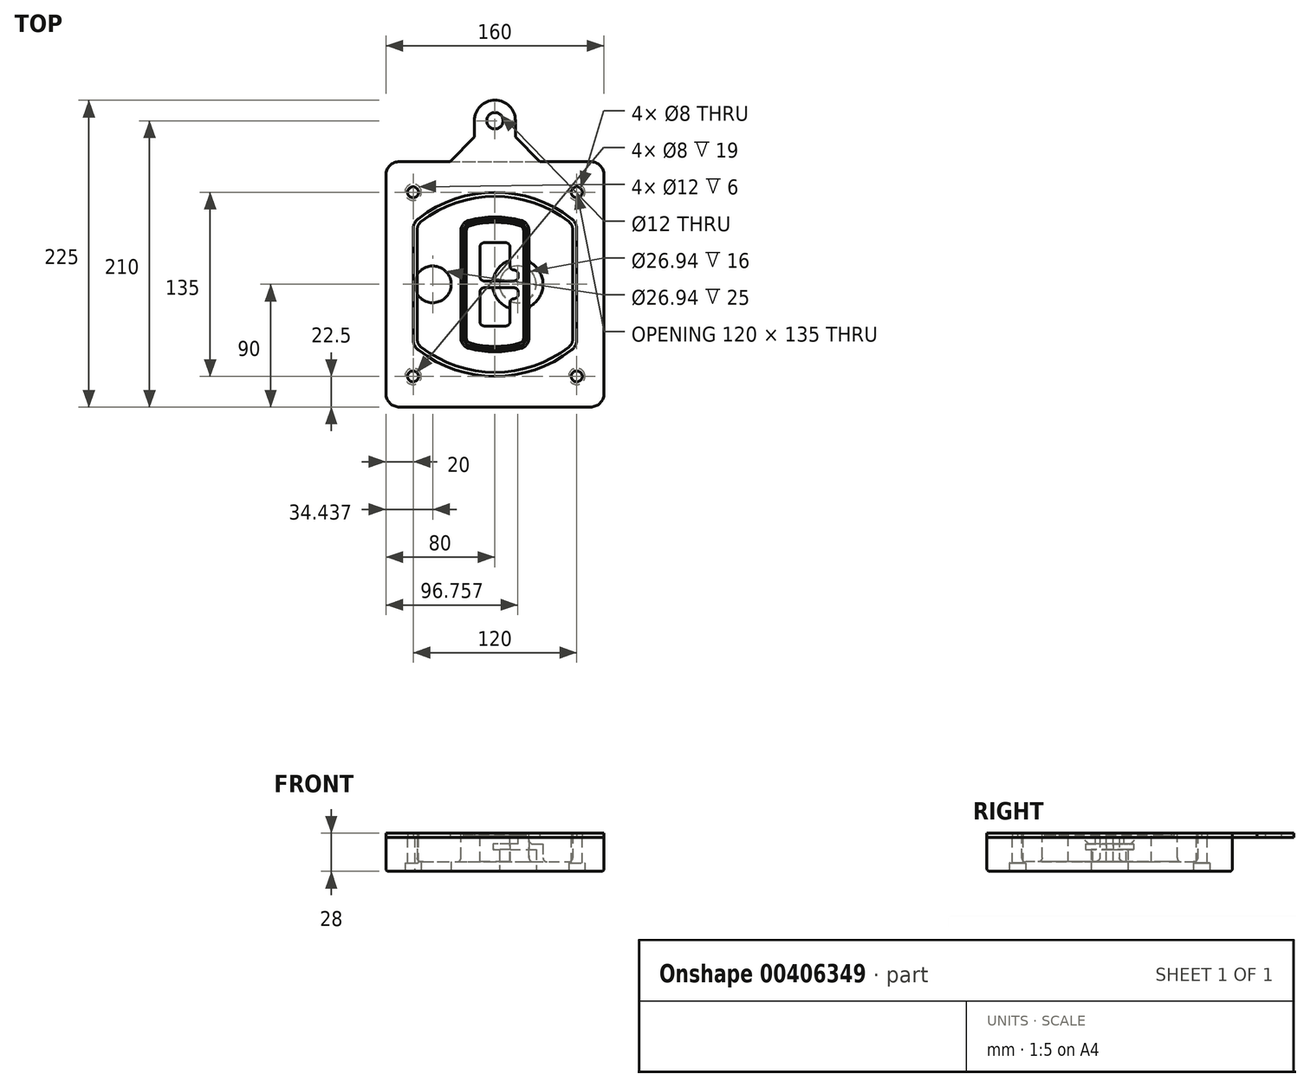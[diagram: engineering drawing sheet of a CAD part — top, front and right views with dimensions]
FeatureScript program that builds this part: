
annotation { "Feature Type Name" : "Feature", "Feature Type Description" : "" }
export const myFeature = defineFeature(function(context is Context, id is Id, definition is map)
    precondition{}
    {
        {
            var Q0;
            Q0=qCreatedBy(makeId("Top.planeOp"),FACE);
            var sketch = newSketch(context, id + "F0", { "sketchPlane" : qUnion([Q0])});
            skPoint(sketch, "E0.rect.middle", {"position": v(0, 0) * mm});
            skLineSegment(sketch, "E1.bottom", {"start": v(-70, -90) * mm, "end": v(70, -90) * mm});
            skLineSegment(sketch, "E1.top", {"start": v(-70, 90) * mm, "end": v(70, 90) * mm});
            skLineSegment(sketch, "E1.left", {"start": v(-80, -80) * mm, "end": v(-80, 80) * mm});
            skLineSegment(sketch, "E1.right", {"start": v(80, -80) * mm, "end": v(80, 80) * mm});
            skLineSegment(sketch, "E2", {"start": v(-80, 90) * mm, "end": v(80, -90) * mm, "construction": true});
            skLineSegment(sketch, "E3", {"start": v(80, 90) * mm, "end": v(-80, -90) * mm, "construction": true});
            skCircle(sketch, "E4", {"center": v(-60, 67.5) * mm, "radius": 4 * mm});
            skCircle(sketch, "E5", {"center": v(60, 67.5) * mm, "radius": 4 * mm});
            skCircle(sketch, "E6", {"center": v(60, -67.5) * mm, "radius": 4 * mm});
            skCircle(sketch, "E7", {"center": v(-60, -67.5) * mm, "radius": 4 * mm});
            skLineSegment(sketch, "E8", {"start": v(-60, 67.5) * mm, "end": v(60, 67.5) * mm, "construction": true});
            skLineSegment(sketch, "E9", {"start": v(60, 67.5) * mm, "end": v(60, -67.5) * mm, "construction": true});
            skLineSegment(sketch, "E10", {"start": v(60, -67.5) * mm, "end": v(-60, -67.5) * mm, "construction": true});
            skLineSegment(sketch, "E11", {"start": v(-60, -67.5) * mm, "end": v(-60, 67.5) * mm, "construction": true});
            skLineSegment(sketch, "E12", {"start": v(-60, 40.3) * mm, "end": v(-60, -40.3) * mm});
            skLineSegment(sketch, "E13", {"start": v(60, 40.3) * mm, "end": v(60, -40.3) * mm});
            skArc(sketch, "E14", {"start": v(56.15, 48.18) * mm, "mid": v(0, 67.5) * mm, "end": v(-56.15, 48.18) * mm});
            skArc(sketch, "E15", {"start": v(-56.15, -48.18) * mm, "mid": v(0, -67.5) * mm, "end": v(56.15, -48.18) * mm});
            skLineSegment(sketch, "E16", {"start": v(-60, 0) * mm, "end": v(60, 0) * mm, "construction": true});
            skPoint(sketch, "E17.visualSharp", {"position": v(-60, -45) * mm});
            skArc(sketch, "E17.filletArc", {"start": v(-60, -40.3) * mm, "mid": v(-58.99, -44.68) * mm, "end": v(-56.15, -48.18) * mm});
            skPoint(sketch, "E18.visualSharp", {"position": v(-60, 45) * mm});
            skArc(sketch, "E18.filletArc", {"start": v(-56.15, 48.18) * mm, "mid": v(-58.99, 44.68) * mm, "end": v(-60, 40.3) * mm});
            skPoint(sketch, "E19.visualSharp", {"position": v(60, 45) * mm});
            skArc(sketch, "E19.filletArc", {"start": v(60, 40.3) * mm, "mid": v(58.99, 44.68) * mm, "end": v(56.15, 48.18) * mm});
            skPoint(sketch, "E20.visualSharp", {"position": v(60, -45) * mm});
            skArc(sketch, "E20.filletArc", {"start": v(56.15, -48.18) * mm, "mid": v(58.99, -44.68) * mm, "end": v(60, -40.3) * mm});
            skPoint(sketch, "E21.visualSharp", {"position": v(-80, 90) * mm});
            skArc(sketch, "E21.filletArc", {"start": v(-70, 90) * mm, "mid": v(-77.07, 87.07) * mm, "end": v(-80, 80) * mm});
            skPoint(sketch, "E22.visualSharp", {"position": v(80, 90) * mm});
            skArc(sketch, "E22.filletArc", {"start": v(80, 80) * mm, "mid": v(77.07, 87.07) * mm, "end": v(70, 90) * mm});
            skPoint(sketch, "E23.visualSharp", {"position": v(80, -90) * mm});
            skArc(sketch, "E23.filletArc", {"start": v(70, -90) * mm, "mid": v(77.07, -87.07) * mm, "end": v(80, -80) * mm});
            skPoint(sketch, "E24.visualSharp", {"position": v(-80, -90) * mm});
            skArc(sketch, "E24.filletArc", {"start": v(-80, -80) * mm, "mid": v(-77.07, -87.07) * mm, "end": v(-70, -90) * mm});
            skArc(sketch, "E25.0", {"start": v(57, 40.3) * mm, "mid": v(56.3, 43.36) * mm, "end": v(54.3, 45.81) * mm});
            skLineSegment(sketch, "E25.1", {"start": v(57, 40.3) * mm, "end": v(57, -40.3) * mm});
            skArc(sketch, "E25.2", {"start": v(54.3, -45.81) * mm, "mid": v(56.3, -43.36) * mm, "end": v(57, -40.3) * mm});
            skArc(sketch, "E25.3", {"start": v(-54.3, -45.81) * mm, "mid": v(0, -64.5) * mm, "end": v(54.3, -45.81) * mm});
            skArc(sketch, "E25.4", {"start": v(-57, -40.3) * mm, "mid": v(-56.3, -43.36) * mm, "end": v(-54.3, -45.81) * mm});
            skArc(sketch, "E25.5", {"start": v(54.3, 45.81) * mm, "mid": v(0, 64.5) * mm, "end": v(-54.3, 45.81) * mm});
            skLineSegment(sketch, "E25.6", {"start": v(-57, 40.3) * mm, "end": v(-57, -40.3) * mm});
            skArc(sketch, "E25.7", {"start": v(-54.3, 45.81) * mm, "mid": v(-56.3, 43.36) * mm, "end": v(-57, 40.3) * mm});
            skArc(sketch, "E26.0", {"start": v(-58.62, 51.33) * mm, "mid": v(-62.58, 46.43) * mm, "end": v(-64, 40.3) * mm});
            skArc(sketch, "E26.1", {"start": v(58.62, 51.33) * mm, "mid": v(0, 71.5) * mm, "end": v(-58.62, 51.33) * mm});
            skArc(sketch, "E26.2", {"start": v(64, 40.3) * mm, "mid": v(62.58, 46.43) * mm, "end": v(58.62, 51.33) * mm});
            skLineSegment(sketch, "E26.3", {"start": v(64, 40.3) * mm, "end": v(64, -40.3) * mm});
            skArc(sketch, "E26.4", {"start": v(58.62, -51.33) * mm, "mid": v(62.58, -46.43) * mm, "end": v(64, -40.3) * mm});
            skLineSegment(sketch, "E26.5", {"start": v(-64, 40.3) * mm, "end": v(-64, -40.3) * mm});
            skArc(sketch, "E26.6", {"start": v(-58.62, -51.33) * mm, "mid": v(0, -71.5) * mm, "end": v(58.62, -51.33) * mm});
            skArc(sketch, "E26.7", {"start": v(-64, -40.3) * mm, "mid": v(-62.58, -46.43) * mm, "end": v(-58.62, -51.33) * mm});
            skSolve(sketch);
        }
        {
            var Q0;
            Q0=makeQuery(id+"F0.imprint","IMPRINT",FACE,{"disambiguationData":[TD([[makeQuery(id+"F0.imprint","IMPRINT",EDGE,{"derivedFrom":sQuery(id+"F0.wireOp",EDGE,"E1.bottom")}),1.0]])]});
            var Q1;
            Q1=makeQuery(id+"F0.imprint","IMPRINT",FACE,{"disambiguationData":[TD([[makeQuery(id+"F0.imprint","IMPRINT",EDGE,{"derivedFrom":sQuery(id+"F0.wireOp",EDGE,"E12")}),1.0]])]});
            var Q2;
            Q2=makeQuery(id+"F0.imprint","IMPRINT",FACE,{"disambiguationData":[TD([[makeQuery(id+"F0.imprint","IMPRINT",EDGE,{"derivedFrom":sQuery(id+"F0.wireOp",EDGE,"E25.0")}),1.0]])]});
            var Q3;
            Q3=makeQuery(id+"F0.imprint","IMPRINT",FACE,{"disambiguationData":[TD([[makeQuery(id+"F0.imprint","IMPRINT",EDGE,{"derivedFrom":sQuery(id+"F0.wireOp",EDGE,"E12")}),-1.0]])]});
            extrude(context, id + "F1", {"entities" : qUnion([Q0, Q1, Q2, Q3]), "oppositeDirection" : true, "depth" : 25 * mm});
        }
        {
            var Q0;
            Q0=makeQuery(id+"F0.imprint","IMPRINT",FACE,{"disambiguationData":[TD([[makeQuery(id+"F0.imprint","IMPRINT",EDGE,{"derivedFrom":sQuery(id+"F0.wireOp",EDGE,"E12")}),1.0]])]});
            var Q1;
            Q1 = qSketchRegion(id + "F16", true);
            extrude(context, id + "F2", {"entities" : qUnion([Q0, Q1]), "operationType" : NewBodyOperationType.ADD, "depth" : 3 * mm});
        }
        {
            var Q0;
            Q0=makeQuery(id+"F0.imprint","IMPRINT",FACE,{"disambiguationData":[TD([[makeQuery(id+"F0.imprint","IMPRINT",EDGE,{"derivedFrom":sQuery(id+"F0.wireOp",EDGE,"E25.0")}),1.0]])]});
            extrude(context, id + "F3", {"entities" : qUnion([Q0]), "operationType" : NewBodyOperationType.REMOVE, "oppositeDirection" : true, "depth" : 18 * mm});
        }
        {
            var Q0;
            Q0=makeQuery(id+"F2.opExtrude","CAP_FACE",FACE,{"disambiguationData":[OSD([sQuery(id+"F0.wireOp",EDGE,"E12"),sQuery(id+"F0.wireOp",EDGE,"E13"),sQuery(id+"F0.wireOp",EDGE,"E14"),sQuery(id+"F0.wireOp",EDGE,"E15"),sQuery(id+"F0.wireOp",EDGE,"E17.filletArc"),sQuery(id+"F0.wireOp",EDGE,"E18.filletArc"),sQuery(id+"F0.wireOp",EDGE,"E19.filletArc"),sQuery(id+"F0.wireOp",EDGE,"E20.filletArc"),sQuery(id+"F0.wireOp",EDGE,"E25.0"),sQuery(id+"F0.wireOp",EDGE,"E25.1"),sQuery(id+"F0.wireOp",EDGE,"E25.2"),sQuery(id+"F0.wireOp",EDGE,"E25.3"),sQuery(id+"F0.wireOp",EDGE,"E25.4"),sQuery(id+"F0.wireOp",EDGE,"E25.5"),sQuery(id+"F0.wireOp",EDGE,"E25.6"),sQuery(id+"F0.wireOp",EDGE,"E25.7")])],"isStart":false});
            var sketch = newSketch(context, id + "F4", { "sketchPlane" : qUnion([Q0])});
            skArc(sketch, "E27.0", {"start": v(-19.08, -46.97) * mm, "mid": v(0, -49.5) * mm, "end": v(19.08, -46.97) * mm});
            skArc(sketch, "E28.0", {"start": v(19.08, 46.97) * mm, "mid": v(0, 49.5) * mm, "end": v(-19.08, 46.97) * mm});
            skLineSegment(sketch, "E29", {"start": v(-25, 39.25) * mm, "end": v(-25, -39.25) * mm});
            skLineSegment(sketch, "E30", {"start": v(25, 39.25) * mm, "end": v(25, -39.25) * mm});
            skLineSegment(sketch, "E31", {"start": v(-25, 45.1) * mm, "end": v(25, 45.1) * mm, "construction": true});
            skLineSegment(sketch, "E32", {"start": v(-25, -45.1) * mm, "end": v(25, -45.1) * mm, "construction": true});
            skPoint(sketch, "E33.visualSharp", {"position": v(-25, 45.1) * mm});
            skArc(sketch, "E33.filletArc", {"start": v(-19.08, 46.97) * mm, "mid": v(-23.35, 44.11) * mm, "end": v(-25, 39.25) * mm});
            skPoint(sketch, "E34.visualSharp", {"position": v(25, 45.1) * mm});
            skArc(sketch, "E34.filletArc", {"start": v(25, 39.25) * mm, "mid": v(23.35, 44.11) * mm, "end": v(19.08, 46.97) * mm});
            skPoint(sketch, "E35.visualSharp", {"position": v(25, -45.1) * mm});
            skArc(sketch, "E35.filletArc", {"start": v(19.08, -46.97) * mm, "mid": v(23.35, -44.11) * mm, "end": v(25, -39.25) * mm});
            skPoint(sketch, "E36.visualSharp", {"position": v(-25, -45.1) * mm});
            skArc(sketch, "E36.filletArc", {"start": v(-25, -39.25) * mm, "mid": v(-23.35, -44.11) * mm, "end": v(-19.08, -46.97) * mm});
            skArc(sketch, "E37.0", {"start": v(54.3, 45.81) * mm, "mid": v(0, 64.5) * mm, "end": v(-54.3, 45.81) * mm});
            skArc(sketch, "E37.1", {"start": v(-54.3, 45.81) * mm, "mid": v(-56.3, 43.36) * mm, "end": v(-57, 40.3) * mm});
            skLineSegment(sketch, "E37.2", {"start": v(-57, 40.3) * mm, "end": v(-57, -40.3) * mm});
            skArc(sketch, "E37.3", {"start": v(-57, -40.3) * mm, "mid": v(-56.3, -43.36) * mm, "end": v(-54.3, -45.81) * mm});
            skArc(sketch, "E37.4", {"start": v(-54.3, -45.81) * mm, "mid": v(0, -64.5) * mm, "end": v(54.3, -45.81) * mm});
            skArc(sketch, "E37.5", {"start": v(54.3, -45.81) * mm, "mid": v(56.3, -43.36) * mm, "end": v(57, -40.3) * mm});
            skLineSegment(sketch, "E37.6", {"start": v(57, 40.3) * mm, "end": v(57, -40.3) * mm});
            skArc(sketch, "E37.7", {"start": v(57, 40.3) * mm, "mid": v(56.3, 43.36) * mm, "end": v(54.3, 45.81) * mm});
            skLineSegment(sketch, "E38.0", {"start": v(23, 39.25) * mm, "end": v(23, -39.25) * mm});
            skArc(sketch, "E38.1", {"start": v(18.56, -45.04) * mm, "mid": v(21.76, -42.9) * mm, "end": v(23, -39.25) * mm});
            skArc(sketch, "E38.2", {"start": v(-18.56, -45.04) * mm, "mid": v(0, -47.5) * mm, "end": v(18.56, -45.04) * mm});
            skArc(sketch, "E38.3", {"start": v(-23, -39.25) * mm, "mid": v(-21.76, -42.9) * mm, "end": v(-18.56, -45.04) * mm});
            skLineSegment(sketch, "E38.4", {"start": v(-23, 39.25) * mm, "end": v(-23, -39.25) * mm});
            skArc(sketch, "E38.5", {"start": v(23, 39.25) * mm, "mid": v(21.76, 42.9) * mm, "end": v(18.56, 45.04) * mm});
            skArc(sketch, "E38.6", {"start": v(-18.56, 45.04) * mm, "mid": v(-21.76, 42.9) * mm, "end": v(-23, 39.25) * mm});
            skArc(sketch, "E38.7", {"start": v(18.56, 45.04) * mm, "mid": v(0, 47.5) * mm, "end": v(-18.56, 45.04) * mm});
            skArc(sketch, "E39.0", {"start": v(21, 39.25) * mm, "mid": v(20.18, 41.68) * mm, "end": v(18.04, 43.1) * mm});
            skLineSegment(sketch, "E39.1", {"start": v(21, 39.25) * mm, "end": v(21, -39.25) * mm});
            skArc(sketch, "E39.2", {"start": v(18.04, -43.1) * mm, "mid": v(20.18, -41.68) * mm, "end": v(21, -39.25) * mm});
            skArc(sketch, "E39.3", {"start": v(-18.04, -43.1) * mm, "mid": v(0, -45.5) * mm, "end": v(18.04, -43.1) * mm});
            skArc(sketch, "E39.4", {"start": v(-21, -39.25) * mm, "mid": v(-20.18, -41.68) * mm, "end": v(-18.04, -43.1) * mm});
            skArc(sketch, "E39.5", {"start": v(18.04, 43.1) * mm, "mid": v(0, 45.5) * mm, "end": v(-18.04, 43.1) * mm});
            skLineSegment(sketch, "E39.6", {"start": v(-21, 39.25) * mm, "end": v(-21, -39.25) * mm});
            skArc(sketch, "E39.7", {"start": v(-18.04, 43.1) * mm, "mid": v(-20.18, 41.68) * mm, "end": v(-21, 39.25) * mm});
            skLineSegment(sketch, "E40", {"start": v(-25, 0) * mm, "end": v(25, 0) * mm, "construction": true});
            skLineSegment(sketch, "E41", {"start": v(-11, 5.5) * mm, "end": v(-11, 27.5) * mm});
            skLineSegment(sketch, "E42", {"start": v(-8, 30.5) * mm, "end": v(8, 30.5) * mm});
            skLineSegment(sketch, "E43", {"start": v(11, 27.5) * mm, "end": v(11, 13.5) * mm});
            skLineSegment(sketch, "E44", {"start": v(14, 10.5) * mm, "end": v(14, 10.5) * mm});
            skLineSegment(sketch, "E45", {"start": v(17, 7.5) * mm, "end": v(17, 5.5) * mm});
            skLineSegment(sketch, "E46", {"start": v(14, 2.5) * mm, "end": v(-8, 2.5) * mm});
            skPoint(sketch, "E47.visualSharp", {"position": v(-11, 30.5) * mm});
            skArc(sketch, "E47.filletArc", {"start": v(-8, 30.5) * mm, "mid": v(-10.12, 29.62) * mm, "end": v(-11, 27.5) * mm});
            skPoint(sketch, "E48.visualSharp", {"position": v(11, 30.5) * mm});
            skArc(sketch, "E48.filletArc", {"start": v(11, 27.5) * mm, "mid": v(10.12, 29.62) * mm, "end": v(8, 30.5) * mm});
            skPoint(sketch, "E49.visualSharp", {"position": v(11, 10.5) * mm});
            skArc(sketch, "E49.filletArc", {"start": v(11, 13.5) * mm, "mid": v(11.88, 11.38) * mm, "end": v(14, 10.5) * mm});
            skPoint(sketch, "E50.visualSharp", {"position": v(17, 10.5) * mm});
            skArc(sketch, "E50.filletArc", {"start": v(17, 7.5) * mm, "mid": v(16.12, 9.62) * mm, "end": v(14, 10.5) * mm});
            skPoint(sketch, "E51.visualSharp", {"position": v(17, 2.5) * mm});
            skArc(sketch, "E51.filletArc", {"start": v(14, 2.5) * mm, "mid": v(16.12, 3.38) * mm, "end": v(17, 5.5) * mm});
            skPoint(sketch, "E52.visualSharp", {"position": v(-11, 2.5) * mm});
            skArc(sketch, "E52.filletArc", {"start": v(-11, 5.5) * mm, "mid": v(-10.12, 3.38) * mm, "end": v(-8, 2.5) * mm});
            skLineSegment(sketch, "E53.0.MirrorCS", {"start": v(14, -2.5) * mm, "end": v(-8, -2.5) * mm});
            skArc(sketch, "E54.0.MirrorCS", {"start": v(-11, -5.5) * mm, "mid": v(-10.12, -3.38) * mm, "end": v(-8, -2.5) * mm});
            skLineSegment(sketch, "E55.0.MirrorCS", {"start": v(-11, -5.5) * mm, "end": v(-11, -27.5) * mm});
            skArc(sketch, "E56.0.MirrorCS", {"start": v(-8, -30.5) * mm, "mid": v(-10.12, -29.62) * mm, "end": v(-11, -27.5) * mm});
            skLineSegment(sketch, "E57.0.MirrorCS", {"start": v(-8, -30.5) * mm, "end": v(8, -30.5) * mm});
            skArc(sketch, "E58.0.MirrorCS", {"start": v(11, -27.5) * mm, "mid": v(10.12, -29.62) * mm, "end": v(8, -30.5) * mm});
            skLineSegment(sketch, "E59.0.MirrorCS", {"start": v(11, -27.5) * mm, "end": v(11, -13.5) * mm});
            skArc(sketch, "E60.0.MirrorCS", {"start": v(11, -13.5) * mm, "mid": v(11.88, -11.38) * mm, "end": v(14, -10.5) * mm});
            skArc(sketch, "E61.0.MirrorCS", {"start": v(17, -7.5) * mm, "mid": v(16.12, -9.62) * mm, "end": v(14, -10.5) * mm});
            skLineSegment(sketch, "E62.0.MirrorCS", {"start": v(17, -7.5) * mm, "end": v(17, -5.5) * mm});
            skArc(sketch, "E63.0.MirrorCS", {"start": v(14, -2.5) * mm, "mid": v(16.12, -3.38) * mm, "end": v(17, -5.5) * mm});
            skSolve(sketch);
        }
        {
            var Q0;
            Q0=makeQuery(id+"F4.imprint","IMPRINT",FACE,{"disambiguationData":[TD([[makeQuery(id+"F4.imprint","IMPRINT",EDGE,{"derivedFrom":sQuery(id+"F4.wireOp",EDGE,"E27.0")}),1.0]])]});
            var Q1;
            Q1=makeQuery(id+"F4.imprint","IMPRINT",FACE,{"disambiguationData":[TD([[makeQuery(id+"F4.imprint","IMPRINT",EDGE,{"derivedFrom":sQuery(id+"F4.wireOp",EDGE,"E38.0")}),-1.0]])]});
            var Q2;
            Q2=makeQuery(id+"F4.imprint","IMPRINT",FACE,{"disambiguationData":[TD([[makeQuery(id+"F4.imprint","IMPRINT",EDGE,{"derivedFrom":sQuery(id+"F4.wireOp",EDGE,"E39.0")}),1.0]])]});
            extrude(context, id + "F5", {"entities" : qUnion([Q0, Q1, Q2]), "operationType" : NewBodyOperationType.ADD, "endBound" : BoundingType.UP_TO_NEXT, "oppositeDirection" : true, "depth" : 25 * mm});
        }
        {
            var Q0;
            Q0=makeQuery(id+"F4.imprint","IMPRINT",FACE,{"disambiguationData":[TD([[makeQuery(id+"F4.imprint","IMPRINT",EDGE,{"derivedFrom":sQuery(id+"F4.wireOp",EDGE,"E38.0")}),-1.0]])]});
            extrude(context, id + "F6", {"entities" : qUnion([Q0]), "operationType" : NewBodyOperationType.REMOVE, "oppositeDirection" : true, "depth" : 2 * mm});
        }
        {
            var Q0;
            Q0=makeQuery(id+"F1.opExtrude","CAP_FACE",FACE,{"disambiguationData":[OSD([sQuery(id+"F0.wireOp",EDGE,"E1.bottom"),sQuery(id+"F0.wireOp",EDGE,"E1.top"),sQuery(id+"F0.wireOp",EDGE,"E1.left"),sQuery(id+"F0.wireOp",EDGE,"E1.right"),sQuery(id+"F0.wireOp",EDGE,"E4"),sQuery(id+"F0.wireOp",EDGE,"E5"),sQuery(id+"F0.wireOp",EDGE,"E6"),sQuery(id+"F0.wireOp",EDGE,"E7"),sQuery(id+"F0.wireOp",EDGE,"E21.filletArc"),sQuery(id+"F0.wireOp",EDGE,"E22.filletArc"),sQuery(id+"F0.wireOp",EDGE,"E23.filletArc"),sQuery(id+"F0.wireOp",EDGE,"E24.filletArc")])],"isStart":false});
            var sketch = newSketch(context, id + "F7", { "sketchPlane" : qUnion([Q0])});
            skCircle(sketch, "E64", {"center": v(16.76, 0) * mm, "radius": 13.47 * mm});
            skCircle(sketch, "E65", {"center": v(-45.56, 0) * mm, "radius": 13.47 * mm});
            skLineSegment(sketch, "E66", {"start": v(80, 0) * mm, "end": v(-80, 0) * mm});
            skCircle(sketch, "E67", {"center": v(16.76, 0) * mm, "radius": 18.47 * mm});
            skCircle(sketch, "E68", {"center": v(60, -67.5) * mm, "radius": 6 * mm});
            skCircle(sketch, "E69", {"center": v(-60, -67.5) * mm, "radius": 6 * mm});
            skCircle(sketch, "E70", {"center": v(-60, 67.5) * mm, "radius": 6 * mm});
            skCircle(sketch, "E71", {"center": v(60, 67.5) * mm, "radius": 6 * mm});
            skSolve(sketch);
        }
        {
            var Q0;
            {var subQ1=sQuery(id+"F7.wireOp",EDGE,"E66");var subQ4=sQuery(id+"F7.wireOp",EDGE,"E64");var subQ6=makeQuery(id+"F7.imprint","INTERSECT",VERTEX,{"disambiguationData":[OD(0.0)],"derivedFrom":[subQ4,subQ1]});Q0=makeQuery(id+"F7.imprint","IMPRINT",FACE,{"disambiguationData":[TD([[makeQuery(id+"F7.imprint","IMPRINT",EDGE,{"disambiguationData":[TD([[subQ6,-1.0]])],"derivedFrom":subQ4}),-1.0]])]});}
            var Q1;
            {var subQ0=sQuery(id+"F7.wireOp",EDGE,"E66");var subQ1=sQuery(id+"F7.wireOp",EDGE,"E64");var subQ3=makeQuery(id+"F7.imprint","INTERSECT",VERTEX,{"disambiguationData":[OD(0.0)],"derivedFrom":[subQ1,subQ0]});Q1=makeQuery(id+"F7.imprint","IMPRINT",FACE,{"disambiguationData":[TD([[makeQuery(id+"F7.imprint","IMPRINT",EDGE,{"disambiguationData":[TD([[subQ3,-1.0]])],"derivedFrom":subQ1}),1.0]])]});}
            var Q2;
            {var subQ0=sQuery(id+"F7.wireOp",EDGE,"E66");var subQ1=sQuery(id+"F7.wireOp",EDGE,"E64");var subQ3=makeQuery(id+"F7.imprint","INTERSECT",VERTEX,{"disambiguationData":[OD(0.0)],"derivedFrom":[subQ1,subQ0]});Q2=makeQuery(id+"F7.imprint","IMPRINT",FACE,{"disambiguationData":[TD([[makeQuery(id+"F7.imprint","IMPRINT",EDGE,{"disambiguationData":[TD([[subQ3,1.0]])],"derivedFrom":subQ1}),1.0]])]});}
            var Q3;
            {var subQ1=sQuery(id+"F7.wireOp",EDGE,"E66");var subQ4=sQuery(id+"F7.wireOp",EDGE,"E64");var subQ6=makeQuery(id+"F7.imprint","INTERSECT",VERTEX,{"disambiguationData":[OD(0.0)],"derivedFrom":[subQ4,subQ1]});Q3=makeQuery(id+"F7.imprint","IMPRINT",FACE,{"disambiguationData":[TD([[makeQuery(id+"F7.imprint","IMPRINT",EDGE,{"disambiguationData":[TD([[subQ6,1.0]])],"derivedFrom":subQ4}),-1.0]])]});}
            extrude(context, id + "F8", {"entities" : qUnion([Q0, Q1, Q2, Q3]), "operationType" : NewBodyOperationType.ADD, "oppositeDirection" : true, "depth" : 20 * mm});
        }
        {
            var Q0;
            {var subQ0=sQuery(id+"F7.wireOp",EDGE,"E66");var subQ1=sQuery(id+"F7.wireOp",EDGE,"E64");var subQ3=makeQuery(id+"F7.imprint","INTERSECT",VERTEX,{"disambiguationData":[OD(0.0)],"derivedFrom":[subQ1,subQ0]});Q0=makeQuery(id+"F7.imprint","IMPRINT",FACE,{"disambiguationData":[TD([[makeQuery(id+"F7.imprint","IMPRINT",EDGE,{"disambiguationData":[TD([[subQ3,-1.0]])],"derivedFrom":subQ1}),1.0]])]});}
            var Q1;
            {var subQ0=sQuery(id+"F7.wireOp",EDGE,"E66");var subQ1=sQuery(id+"F7.wireOp",EDGE,"E64");var subQ3=makeQuery(id+"F7.imprint","INTERSECT",VERTEX,{"disambiguationData":[OD(0.0)],"derivedFrom":[subQ1,subQ0]});Q1=makeQuery(id+"F7.imprint","IMPRINT",FACE,{"disambiguationData":[TD([[makeQuery(id+"F7.imprint","IMPRINT",EDGE,{"disambiguationData":[TD([[subQ3,1.0]])],"derivedFrom":subQ1}),1.0]])]});}
            extrude(context, id + "F9", {"entities" : qUnion([Q0, Q1]), "operationType" : NewBodyOperationType.REMOVE, "oppositeDirection" : true, "depth" : 16 * mm});
        }
        {
            var Q0;
            {var subQ0=sQuery(id+"F7.wireOp",EDGE,"E66");var subQ1=sQuery(id+"F7.wireOp",EDGE,"E65");var subQ3=makeQuery(id+"F7.imprint","INTERSECT",VERTEX,{"disambiguationData":[OD(0.0)],"derivedFrom":[subQ1,subQ0]});Q0=makeQuery(id+"F7.imprint","IMPRINT",FACE,{"disambiguationData":[TD([[makeQuery(id+"F7.imprint","IMPRINT",EDGE,{"disambiguationData":[TD([[subQ3,-1.0]])],"derivedFrom":subQ1}),1.0]])]});}
            var Q1;
            {var subQ0=sQuery(id+"F7.wireOp",EDGE,"E66");var subQ1=sQuery(id+"F7.wireOp",EDGE,"E65");var subQ3=makeQuery(id+"F7.imprint","INTERSECT",VERTEX,{"disambiguationData":[OD(0.0)],"derivedFrom":[subQ1,subQ0]});Q1=makeQuery(id+"F7.imprint","IMPRINT",FACE,{"disambiguationData":[TD([[makeQuery(id+"F7.imprint","IMPRINT",EDGE,{"disambiguationData":[TD([[subQ3,1.0]])],"derivedFrom":subQ1}),1.0]])]});}
            extrude(context, id + "F10", {"entities" : qUnion([Q0, Q1]), "operationType" : NewBodyOperationType.REMOVE, "oppositeDirection" : true, "depth" : 25 * mm});
        }
        {
            var Q0;
            Q0=makeQuery(id+"F7.imprint","IMPRINT",FACE,{"disambiguationData":[TD([[makeQuery(id+"F7.imprint","IMPRINT",EDGE,{"derivedFrom":sQuery(id+"F7.wireOp",EDGE,"E68")}),1.0]])]});
            var Q1;
            Q1=makeQuery(id+"F7.imprint","IMPRINT",FACE,{"disambiguationData":[TD([[makeQuery(id+"F7.imprint","IMPRINT",EDGE,{"derivedFrom":makeQuery(id+"F1.opExtrude","CAP_EDGE",EDGE,{"disambiguationData":[OSD([sQuery(id+"F0.wireOp",EDGE,"E5")])],"isStart":false})}),-1.0]])]});
            var Q2;
            Q2=makeQuery(id+"F7.imprint","IMPRINT",FACE,{"disambiguationData":[TD([[makeQuery(id+"F7.imprint","IMPRINT",EDGE,{"derivedFrom":sQuery(id+"F7.wireOp",EDGE,"E69")}),1.0]])]});
            var Q3;
            Q3=makeQuery(id+"F7.imprint","IMPRINT",FACE,{"disambiguationData":[TD([[makeQuery(id+"F7.imprint","IMPRINT",EDGE,{"derivedFrom":makeQuery(id+"F1.opExtrude","CAP_EDGE",EDGE,{"disambiguationData":[OSD([sQuery(id+"F0.wireOp",EDGE,"E4")])],"isStart":false})}),-1.0]])]});
            var Q4;
            Q4=makeQuery(id+"F7.imprint","IMPRINT",FACE,{"disambiguationData":[TD([[makeQuery(id+"F7.imprint","IMPRINT",EDGE,{"derivedFrom":sQuery(id+"F7.wireOp",EDGE,"E70")}),1.0]])]});
            var Q5;
            Q5=makeQuery(id+"F7.imprint","IMPRINT",FACE,{"disambiguationData":[TD([[makeQuery(id+"F7.imprint","IMPRINT",EDGE,{"derivedFrom":makeQuery(id+"F1.opExtrude","CAP_EDGE",EDGE,{"disambiguationData":[OSD([sQuery(id+"F0.wireOp",EDGE,"E7")])],"isStart":false})}),-1.0]])]});
            var Q6;
            Q6=makeQuery(id+"F7.imprint","IMPRINT",FACE,{"disambiguationData":[TD([[makeQuery(id+"F7.imprint","IMPRINT",EDGE,{"derivedFrom":sQuery(id+"F7.wireOp",EDGE,"E71")}),1.0]])]});
            var Q7;
            Q7=makeQuery(id+"F7.imprint","IMPRINT",FACE,{"disambiguationData":[TD([[makeQuery(id+"F7.imprint","IMPRINT",EDGE,{"derivedFrom":makeQuery(id+"F1.opExtrude","CAP_EDGE",EDGE,{"disambiguationData":[OSD([sQuery(id+"F0.wireOp",EDGE,"E6")])],"isStart":false})}),-1.0]])]});
            extrude(context, id + "F11", {"entities" : qUnion([Q0, Q1, Q2, Q3, Q4, Q5, Q6, Q7]), "operationType" : NewBodyOperationType.REMOVE, "oppositeDirection" : true, "depth" : 6 * mm});
        }
        {
            var Q0;
            Q0=makeQuery(id+"F9.boolean.opBoolean","COPY",FACE,{"derivedFrom":makeQuery(id+"F9.opExtrude","CAP_FACE",FACE,{"disambiguationData":[OSD([sQuery(id+"F7.wireOp",EDGE,"E64")])],"isStart":false})});
            var sketch = newSketch(context, id + "F12", { "sketchPlane" : qUnion([Q0])});
            skArc(sketch, "E72.0", {"start": v(11, 17.55) * mm, "mid": v(2.57, 11.82) * mm, "end": v(-1.54, 2.5) * mm});
            skArc(sketch, "E72.1", {"start": v(-1.54, -2.5) * mm, "mid": v(2.57, -11.82) * mm, "end": v(11, -17.55) * mm});
            skLineSegment(sketch, "E73", {"start": v(-1.54, -2.5) * mm, "end": v(14, -2.5) * mm});
            skLineSegment(sketch, "E74.0", {"start": v(14, 2.5) * mm, "end": v(-1.54, 2.5) * mm});
            skArc(sketch, "E74.1", {"start": v(14, 2.5) * mm, "mid": v(16.12, 3.38) * mm, "end": v(17, 5.5) * mm});
            skLineSegment(sketch, "E74.2", {"start": v(17, 7.5) * mm, "end": v(17, 5.5) * mm});
            skArc(sketch, "E74.3", {"start": v(17, 7.5) * mm, "mid": v(16.12, 9.62) * mm, "end": v(14, 10.5) * mm});
            skArc(sketch, "E74.4", {"start": v(11, 13.5) * mm, "mid": v(11.88, 11.38) * mm, "end": v(14, 10.5) * mm});
            skLineSegment(sketch, "E74.5", {"start": v(11, 17.55) * mm, "end": v(11, 13.5) * mm});
            skLineSegment(sketch, "E74.7", {"start": v(14, -2.5) * mm, "end": v(-1.54, -2.5) * mm});
            skArc(sketch, "E74.8", {"start": v(14, -2.5) * mm, "mid": v(16.12, -3.38) * mm, "end": v(17, -5.5) * mm});
            skLineSegment(sketch, "E74.9", {"start": v(17, -7.5) * mm, "end": v(17, -5.5) * mm});
            skArc(sketch, "E74.10", {"start": v(17, -7.5) * mm, "mid": v(16.12, -9.62) * mm, "end": v(14, -10.5) * mm});
            skArc(sketch, "E74.11", {"start": v(11, -13.5) * mm, "mid": v(11.88, -11.38) * mm, "end": v(14, -10.5) * mm});
            skLineSegment(sketch, "E74.12", {"start": v(11, -17.55) * mm, "end": v(11, -13.5) * mm});
            skPoint(sketch, "E75.orphan", {"position": v(11, -27.5) * mm});
            skPoint(sketch, "E76.orphan", {"position": v(-8, -2.5) * mm});
            skPoint(sketch, "E77.orphan", {"position": v(-8, 2.5) * mm});
            skPoint(sketch, "E78.orphan", {"position": v(11, 27.5) * mm});
            skSolve(sketch);
        }
        {
            var Q0;
            {var subQ7=sQuery(id+"F12.wireOp",EDGE,"E72.0");var subQ14=sQuery(id+"F12.wireOp",EDGE,"E72.1");var subQ16=sQuery(id+"F12.wireOp",EDGE,"E74.1");var subQ18=sQuery(id+"F12.wireOp",EDGE,"E74.8");Q0=qUnion([makeQuery(id+"F12.imprint","IMPRINT",FACE,{"disambiguationData":[TD([[makeQuery(id+"F12.imprint","IMPRINT",EDGE,{"derivedFrom":subQ7}),1.0]])]}),makeQuery(id+"F12.imprint","IMPRINT",FACE,{"disambiguationData":[TD([[makeQuery(id+"F12.imprint","IMPRINT",EDGE,{"derivedFrom":subQ14}),1.0]])]}),makeQuery(id+"F12.imprint","IMPRINT",FACE,{"disambiguationData":[TD([[makeQuery(id+"F12.imprint","IMPRINT",EDGE,{"derivedFrom":subQ16}),1.0]])]}),makeQuery(id+"F12.imprint","IMPRINT",FACE,{"disambiguationData":[TD([[makeQuery(id+"F12.imprint","IMPRINT",EDGE,{"derivedFrom":subQ18}),-1.0]])]})]);}
            var Q1;
            Q1=makeQuery(id+"F5.boolean.opBoolean","SPLIT",FACE,{"disambiguationData":[TD([makeQuery(id+"F5.opExtrude","SWEPT_FACE",FACE,{"disambiguationData":[OSD([sQuery(id+"F4.wireOp",EDGE,"E41")])]})])],"derivedFrom":makeQuery(id+"F3.boolean.opBoolean","COPY",FACE,{"derivedFrom":makeQuery(id+"F3.opExtrude","CAP_FACE",FACE,{"disambiguationData":[OSD([sQuery(id+"F0.wireOp",EDGE,"E25.0"),sQuery(id+"F0.wireOp",EDGE,"E25.1"),sQuery(id+"F0.wireOp",EDGE,"E25.2"),sQuery(id+"F0.wireOp",EDGE,"E25.3"),sQuery(id+"F0.wireOp",EDGE,"E25.4"),sQuery(id+"F0.wireOp",EDGE,"E25.5"),sQuery(id+"F0.wireOp",EDGE,"E25.6"),sQuery(id+"F0.wireOp",EDGE,"E25.7")])],"isStart":false})})});
            extrude(context, id + "F13", {"entities" : qUnion([Q0]), "operationType" : NewBodyOperationType.REMOVE, "endBound" : BoundingType.UP_TO_SURFACE, "endBoundEntityFace" : qUnion([Q1]), "depth" : 25 * mm});
        }
        {
            var Q0;
            Q0=makeQuery(id+"F3.boolean.opBoolean","COPY",EDGE,{"derivedFrom":makeQuery(id+"F3.opExtrude","CAP_EDGE",EDGE,{"disambiguationData":[OSD([sQuery(id+"F0.wireOp",EDGE,"E25.6")])],"isStart":false})});
            var Q1;
            Q1=makeQuery(id+"F8.boolean.opBoolean","INTERSECT",EDGE,{"derivedFrom":[makeQuery(id+"F5.opExtrude","SWEPT_FACE",FACE,{"disambiguationData":[OSD([sQuery(id+"F4.wireOp",EDGE,"E30")])]}),makeQuery(id+"F8.opExtrude","CAP_FACE",FACE,{"disambiguationData":[OSD([sQuery(id+"F7.wireOp",EDGE,"E67")])],"isStart":false})]});
            var Q2;
            Q2=makeQuery(id+"F8.boolean.opBoolean","INTERSECT",EDGE,{"disambiguationData":[OD(1.0)],"derivedFrom":[makeQuery(id+"F5.opExtrude","SWEPT_FACE",FACE,{"disambiguationData":[OSD([sQuery(id+"F4.wireOp",EDGE,"E30")])]}),makeQuery(id+"F8.opExtrude","SWEPT_FACE",FACE,{"disambiguationData":[OSD([sQuery(id+"F7.wireOp",EDGE,"E67")])]})]});
            var Q3;
            {var subQ0=sQuery(id+"F4.wireOp",EDGE,"E30");Q3=makeQuery(id+"F8.boolean.opBoolean","SPLIT",EDGE,{"disambiguationData":[TD([makeQuery(id+"F5.opExtrude","SWEPT_FACE",FACE,{"disambiguationData":[OSD([sQuery(id+"F4.wireOp",EDGE,"E35.filletArc")])]})])],"derivedFrom":makeQuery(id+"F5.opExtrude","CAP_EDGE",EDGE,{"disambiguationData":[OSD([subQ0])],"isStart":false})});}
            var Q4;
            {var subQ0=sQuery(id+"F0.wireOp",EDGE,"E25.7");var subQ1=sQuery(id+"F0.wireOp",EDGE,"E25.1");var subQ2=sQuery(id+"F0.wireOp",EDGE,"E25.6");var subQ3=sQuery(id+"F0.wireOp",EDGE,"E25.5");var subQ4=sQuery(id+"F0.wireOp",EDGE,"E25.4");var subQ5=sQuery(id+"F0.wireOp",EDGE,"E25.0");var subQ6=sQuery(id+"F0.wireOp",EDGE,"E25.2");var subQ7=sQuery(id+"F0.wireOp",EDGE,"E25.3");Q4=makeQuery(id+"F8.boolean.opBoolean","INTERSECT",EDGE,{"derivedFrom":[makeQuery(id+"F5.boolean.opBoolean","SPLIT",FACE,{"disambiguationData":[TD([makeQuery(id+"F2.opExtrude","SWEPT_FACE",FACE,{"disambiguationData":[OSD([subQ5])]})])],"derivedFrom":makeQuery(id+"F3.boolean.opBoolean","COPY",FACE,{"derivedFrom":makeQuery(id+"F3.opExtrude","CAP_FACE",FACE,{"disambiguationData":[OSD([subQ5,subQ1,subQ6,subQ7,subQ4,subQ3,subQ2,subQ0])],"isStart":false})})}),makeQuery(id+"F8.opExtrude","SWEPT_FACE",FACE,{"disambiguationData":[OSD([sQuery(id+"F7.wireOp",EDGE,"E67")])]})]});}
            var Q5;
            Q5=makeQuery(id+"F8.boolean.opBoolean","INTERSECT",EDGE,{"disambiguationData":[OD(0.0)],"derivedFrom":[makeQuery(id+"F5.opExtrude","SWEPT_FACE",FACE,{"disambiguationData":[OSD([sQuery(id+"F4.wireOp",EDGE,"E30")])]}),makeQuery(id+"F8.opExtrude","SWEPT_FACE",FACE,{"disambiguationData":[OSD([sQuery(id+"F7.wireOp",EDGE,"E67")])]})]});
            fillet(context, id + "F14", {"entities" : qUnion([Q0, Q1, Q2, Q3, Q4, Q5]), "radius" : 3 * mm, "tangentPropagation" : true, "allowEdgeOverflow" : false});
        }
        {
            var Q0;
            Q0=makeQuery(id+"F1.opExtrude","CAP_EDGE",EDGE,{"disambiguationData":[OSD([sQuery(id+"F0.wireOp",EDGE,"E1.bottom")])],"isStart":false});
            fillet(context, id + "F15", {"entities" : qUnion([Q0]), "radius" : 2 * mm, "tangentPropagation" : true, "allowEdgeOverflow" : false});
        }
        {
            var Q0;
            {var subQ0=sQuery(id+"F0.wireOp",EDGE,"E21.filletArc");var subQ1=sQuery(id+"F0.wireOp",EDGE,"E7");var subQ2=sQuery(id+"F0.wireOp",EDGE,"E6");var subQ3=sQuery(id+"F0.wireOp",EDGE,"E5");var subQ4=sQuery(id+"F0.wireOp",EDGE,"E4");var subQ5=sQuery(id+"F0.wireOp",EDGE,"E22.filletArc");var subQ6=sQuery(id+"F0.wireOp",EDGE,"E1.bottom");var subQ7=sQuery(id+"F0.wireOp",EDGE,"E1.right");var subQ8=sQuery(id+"F0.wireOp",EDGE,"E1.top");var subQ9=sQuery(id+"F0.wireOp",EDGE,"E1.left");var subQ10=sQuery(id+"F0.wireOp",EDGE,"E23.filletArc");var subQ11=sQuery(id+"F0.wireOp",EDGE,"E24.filletArc");Q0=makeQuery(id+"F2.boolean.opBoolean","SPLIT",FACE,{"disambiguationData":[TD([makeQuery(id+"F1.opExtrude","SWEPT_FACE",FACE,{"disambiguationData":[OSD([subQ6])]})])],"derivedFrom":makeQuery(id+"F1.opExtrude","CAP_FACE",FACE,{"disambiguationData":[OSD([subQ6,subQ8,subQ9,subQ7,subQ4,subQ3,subQ2,subQ1,subQ0,subQ5,subQ10,subQ11])],"isStart":true})});}
            var sketch = newSketch(context, id + "F16", { "sketchPlane" : qUnion([Q0])});
            skLineSegment(sketch, "E79", {"start": v(-15, 108) * mm, "end": v(-33, 90) * mm});
            skLineSegment(sketch, "E80", {"start": v(33, 90) * mm, "end": v(15, 108) * mm});
            skLineSegment(sketch, "E81", {"start": v(-15, 108) * mm, "end": v(-15, 120) * mm});
            skLineSegment(sketch, "E82", {"start": v(15, 108) * mm, "end": v(15, 120) * mm});
            skArc(sketch, "E83", {"start": v(15, 120) * mm, "mid": v(0, 135) * mm, "end": v(-15, 120) * mm});
            skCircle(sketch, "E84", {"center": v(0, 120) * mm, "radius": 6 * mm});
            skLineSegment(sketch, "E85", {"start": v(0, 120) * mm, "end": v(0, 90) * mm, "construction": true});
            skLineSegment(sketch, "E86", {"start": v(-80, 0) * mm, "end": v(80, 0) * mm, "construction": true});
            skArc(sketch, "E87.MirrorCS", {"start": v(15, -120) * mm, "mid": v(0, -135) * mm, "end": v(-15, -120) * mm});
            skLineSegment(sketch, "E88.MirrorCS", {"start": v(15, -108) * mm, "end": v(15, -120) * mm});
            skLineSegment(sketch, "E89.MirrorCS", {"start": v(-15, -108) * mm, "end": v(-15, -120) * mm});
            skLineSegment(sketch, "E90.MirrorCS", {"start": v(0, -120) * mm, "end": v(0, -90) * mm, "construction": true});
            skCircle(sketch, "E91.MirrorC", {"center": v(0, -120) * mm, "radius": 6 * mm});
            skLineSegment(sketch, "E92.MirrorCS", {"start": v(33, -90) * mm, "end": v(15, -108) * mm});
            skLineSegment(sketch, "E93.MirrorCS", {"start": v(-15, -108) * mm, "end": v(-33, -90) * mm});
            skSolve(sketch);
        }
        {
            var Q0;
            Q0=makeQuery(id+"F16.imprint","IMPRINT",FACE,{"disambiguationData":[TD([[makeQuery(id+"F16.imprint","IMPRINT",EDGE,{"derivedFrom":makeQuery(id+"F1.opExtrude","CAP_EDGE",EDGE,{"disambiguationData":[OSD([sQuery(id+"F0.wireOp",EDGE,"E1.left")])],"isStart":true})}),-1.0]])]});
            var Q1;
            Q1=makeQuery(id+"F16.imprint","IMPRINT",FACE,{"disambiguationData":[TD([[makeQuery(id+"F16.imprint","IMPRINT",EDGE,{"derivedFrom":sQuery(id+"F16.wireOp",EDGE,"E87.MirrorCS")}),-1.0]])]});
            var Q2;
            {var subQ0=sQuery(id+"F16.wireOp",EDGE,"E79");Q2=makeQuery(id+"F16.imprint","IMPRINT",FACE,{"disambiguationData":[TD([[makeQuery(id+"F16.imprint","IMPRINT",EDGE,{"derivedFrom":subQ0}),1.0]])]});}
            extrude(context, id + "F17", {"entities" : qUnion([Q0, Q1, Q2]), "depth" : 3 * mm});
        }
    });
